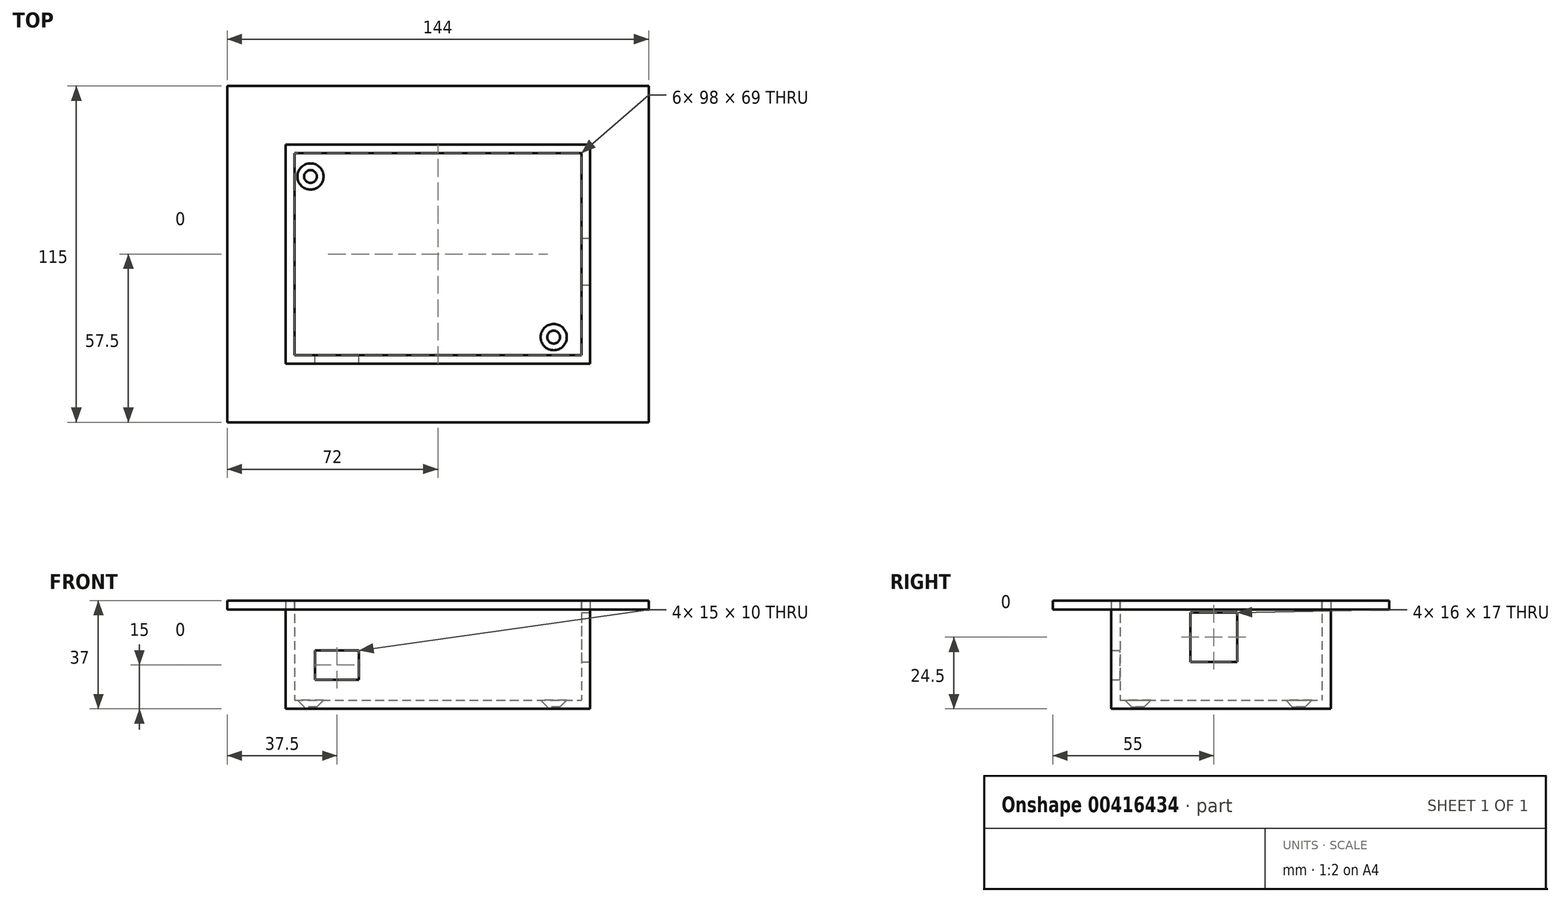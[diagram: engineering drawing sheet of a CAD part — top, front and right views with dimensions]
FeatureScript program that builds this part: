
annotation { "Feature Type Name" : "Feature", "Feature Type Description" : "" }
export const myFeature = defineFeature(function(context is Context, id is Id, definition is map)
    precondition{}
    {
        {
            var Q0;
            Q0=qCreatedBy(makeId("Top.planeOp"),FACE);
            var sketch = newSketch(context, id + "F0", { "sketchPlane" : qUnion([Q0])});
            skLineSegment(sketch, "E0.bottom", {"start": v(0, 0) * mm, "end": v(104, 0) * mm});
            skLineSegment(sketch, "E0.top", {"start": v(0, 75) * mm, "end": v(104, 75) * mm});
            skLineSegment(sketch, "E0.left", {"start": v(0, 0) * mm, "end": v(0, 75) * mm});
            skLineSegment(sketch, "E0.right", {"start": v(104, 0) * mm, "end": v(104, 75) * mm});
            skSolve(sketch);
        }
        {
            var Q0;
            Q0 = qSketchRegion(id + "F0", true);
            extrude(context, id + "F1", {"entities" : qUnion([Q0]), "depth" : 37 * mm});
        }
        {
            var Q0;
            Q0=makeQuery(id+"F1.opExtrude","CAP_FACE",FACE,{"disambiguationData":[OSD([sQuery(id+"F0.wireOp",EDGE,"E0.bottom"),sQuery(id+"F0.wireOp",EDGE,"E0.top"),sQuery(id+"F0.wireOp",EDGE,"E0.left"),sQuery(id+"F0.wireOp",EDGE,"E0.right")])],"isStart":false});
            shell(context, id + "F2", {"entities" : qUnion([Q0]), "thickness" : 3 * mm});
        }
        {
            var Q0;
            Q0=makeQuery(id+"F2.opShell","OFFSET_FACE",FACE,{"disambiguationData":[OSD([sQuery(id+"F0.wireOp",EDGE,"E0.bottom"),sQuery(id+"F0.wireOp",EDGE,"E0.top"),sQuery(id+"F0.wireOp",EDGE,"E0.left"),sQuery(id+"F0.wireOp",EDGE,"E0.right")])]});
            var sketch = newSketch(context, id + "F3", { "sketchPlane" : qUnion([Q0])});
            skPoint(sketch, "E1", {"position": v(8.47, 64.05) * mm});
            skPoint(sketch, "E2", {"position": v(91.56, 9.12) * mm});
            skSolve(sketch);
        }
        {
            var Q0;
            Q0=sQuery(id+"F3.wireOp",VERTEX,"E1");
            var Q1;
            Q1=makeQuery(id+"F1.opExtrude","SWEPT_BODY",BODY,{"disambiguationData":[OSD([sQuery(id+"F0.wireOp",EDGE,"E0.bottom"),sQuery(id+"F0.wireOp",EDGE,"E0.top"),sQuery(id+"F0.wireOp",EDGE,"E0.left"),sQuery(id+"F0.wireOp",EDGE,"E0.right")])]});
            hole(context, id + "F4", {"style" : HoleStyle.C_SINK, "endStyle" : HoleEndStyle.THROUGH, "standardTappedOrClearance" : lookupTablePath({ "standard" : "ISO", "fit" : "Normal", "size" : "M4", "type" : "Clearance" }), "standardBlindInLast" : lookupTablePath({ "fit" : "Standard", "standard" : "ISO", "size" : "M4", "type" : "Clearance" }), "holeDiameter" : 4.4 * mm, "cSinkDiameter" : 8.96 * mm, "cSinkAngle" : 90 * degree, "isTappedThrough" : true, "tappedDepth" : 12 * mm, "tapClearance" : 3, "locations" : qUnion([Q0]), "scope" : qUnion([Q1])});
        }
        {
            var Q0;
            Q0=sQuery(id+"F3.wireOp",VERTEX,"E2");
            var Q1;
            Q1=makeQuery(id+"F1.opExtrude","SWEPT_BODY",BODY,{"disambiguationData":[OSD([sQuery(id+"F0.wireOp",EDGE,"E0.bottom"),sQuery(id+"F0.wireOp",EDGE,"E0.top"),sQuery(id+"F0.wireOp",EDGE,"E0.left"),sQuery(id+"F0.wireOp",EDGE,"E0.right")])]});
            hole(context, id + "F5", {"style" : HoleStyle.C_SINK, "endStyle" : HoleEndStyle.THROUGH, "standardTappedOrClearance" : lookupTablePath({ "standard" : "ISO", "fit" : "Normal", "size" : "M4", "type" : "Clearance" }), "standardBlindInLast" : lookupTablePath({ "fit" : "Standard", "standard" : "ISO", "size" : "M4", "type" : "Clearance" }), "holeDiameter" : 4.4 * mm, "cSinkDiameter" : 8.96 * mm, "cSinkAngle" : 90 * degree, "isTappedThrough" : true, "tappedDepth" : 12 * mm, "tapClearance" : 3, "locations" : qUnion([Q0]), "scope" : qUnion([Q1])});
        }
        {
            var Q0;
            Q0=makeQuery(id+"Fv2Lp8H76RmDUAu_1.boolean.opBoolean","MERGE",FACE,{"derivedFrom":[makeQuery(id+"F2.opShell","OFFSET_FACE",FACE,{"disambiguationData":[OSD([sQuery(id+"F0.wireOp",EDGE,"E0.bottom")])]}),makeQuery(id+"Fv2Lp8H76RmDUAu_1.opExtrude","SWEPT_FACE",FACE,{"disambiguationData":[OSD([sQuery(id+"FU4CP0wZnbrBb0s_1.wireOp",EDGE,"30jitwlD-jqMr-7I8g-f0zv-U9qNJRmIhCNw.top")])]})]});
            var sketch = newSketch(context, id + "F6", { "sketchPlane" : qUnion([Q0])});
            skLineSegment(sketch, "E3.bottom", {"start": v(-10, 10) * mm, "end": v(-25, 10) * mm});
            skLineSegment(sketch, "E3.top", {"start": v(-10, 20) * mm, "end": v(-25, 20) * mm});
            skLineSegment(sketch, "E3.left", {"start": v(-10, 10) * mm, "end": v(-10, 20) * mm});
            skLineSegment(sketch, "E3.right", {"start": v(-25, 10) * mm, "end": v(-25, 20) * mm});
            skSolve(sketch);
        }
        {
            var Q0;
            Q0 = qSketchRegion(id + "F6", true);
            extrude(context, id + "F7", {"entities" : qUnion([Q0]), "operationType" : NewBodyOperationType.REMOVE, "oppositeDirection" : true, "depth" : 4 * mm});
        }
        {
            var Q0;
            Q0=makeQuery(id+"F1.opExtrude","CAP_FACE",FACE,{"disambiguationData":[OSD([sQuery(id+"F0.wireOp",EDGE,"E0.bottom"),sQuery(id+"F0.wireOp",EDGE,"E0.top"),sQuery(id+"F0.wireOp",EDGE,"E0.left"),sQuery(id+"F0.wireOp",EDGE,"E0.right")])],"isStart":false});
            var sketch = newSketch(context, id + "F8", { "sketchPlane" : qUnion([Q0])});
            skLineSegment(sketch, "E4.bottom", {"start": v(-20, 95) * mm, "end": v(124, 95) * mm});
            skLineSegment(sketch, "E4.top", {"start": v(-20, -20) * mm, "end": v(124, -20) * mm});
            skLineSegment(sketch, "E4.left", {"start": v(-20, 95) * mm, "end": v(-20, -20) * mm});
            skLineSegment(sketch, "E4.right", {"start": v(124, 95) * mm, "end": v(124, -20) * mm});
            skSolve(sketch);
        }
        {
            var Q0;
            Q0 = qSketchRegion(id + "F8", true);
            extrude(context, id + "F9", {"entities" : qUnion([Q0]), "oppositeDirection" : true, "depth" : 3 * mm});
        }
        {
            var Q0;
            Q0=makeQuery(id+"F9.opExtrude","CAP_FACE",FACE,{"disambiguationData":[OSD([sQuery(id+"F8.wireOp",EDGE,"E4.bottom"),sQuery(id+"F8.wireOp",EDGE,"E4.top"),sQuery(id+"F8.wireOp",EDGE,"E4.left"),sQuery(id+"F8.wireOp",EDGE,"E4.right")])],"isStart":true});
            var sketch = newSketch(context, id + "F10", { "sketchPlane" : qUnion([Q0])});
            skLineSegment(sketch, "E5.bottom", {"start": v(3, 72) * mm, "end": v(101, 72) * mm});
            skLineSegment(sketch, "E5.top", {"start": v(3, 3) * mm, "end": v(101, 3) * mm});
            skLineSegment(sketch, "E5.left", {"start": v(3, 72) * mm, "end": v(3, 3) * mm});
            skLineSegment(sketch, "E5.right", {"start": v(101, 72) * mm, "end": v(101, 3) * mm});
            skSolve(sketch);
        }
        {
            var Q0;
            Q0 = qSketchRegion(id + "F10", true);
            extrude(context, id + "F11", {"entities" : qUnion([Q0]), "operationType" : NewBodyOperationType.REMOVE, "oppositeDirection" : true, "depth" : 3 * mm});
        }
        {
            var Q0;
            Q0=makeQuery(id+"F1.opExtrude","SWEPT_FACE",FACE,{"disambiguationData":[OSD([sQuery(id+"F0.wireOp",EDGE,"E0.right")])]});
            var sketch = newSketch(context, id + "F12", { "sketchPlane" : qUnion([Q0])});
            skLineSegment(sketch, "E6.bottom", {"start": v(43, 33) * mm, "end": v(27, 33) * mm});
            skLineSegment(sketch, "E6.top", {"start": v(43, 16) * mm, "end": v(27, 16) * mm});
            skLineSegment(sketch, "E6.left", {"start": v(43, 33) * mm, "end": v(43, 16) * mm});
            skLineSegment(sketch, "E6.right", {"start": v(27, 33) * mm, "end": v(27, 16) * mm});
            skSolve(sketch);
        }
        {
            var Q0;
            Q0 = qSketchRegion(id + "F12", true);
            extrude(context, id + "F13", {"entities" : qUnion([Q0]), "operationType" : NewBodyOperationType.REMOVE, "oppositeDirection" : true, "depth" : 3 * mm});
        }
    });
